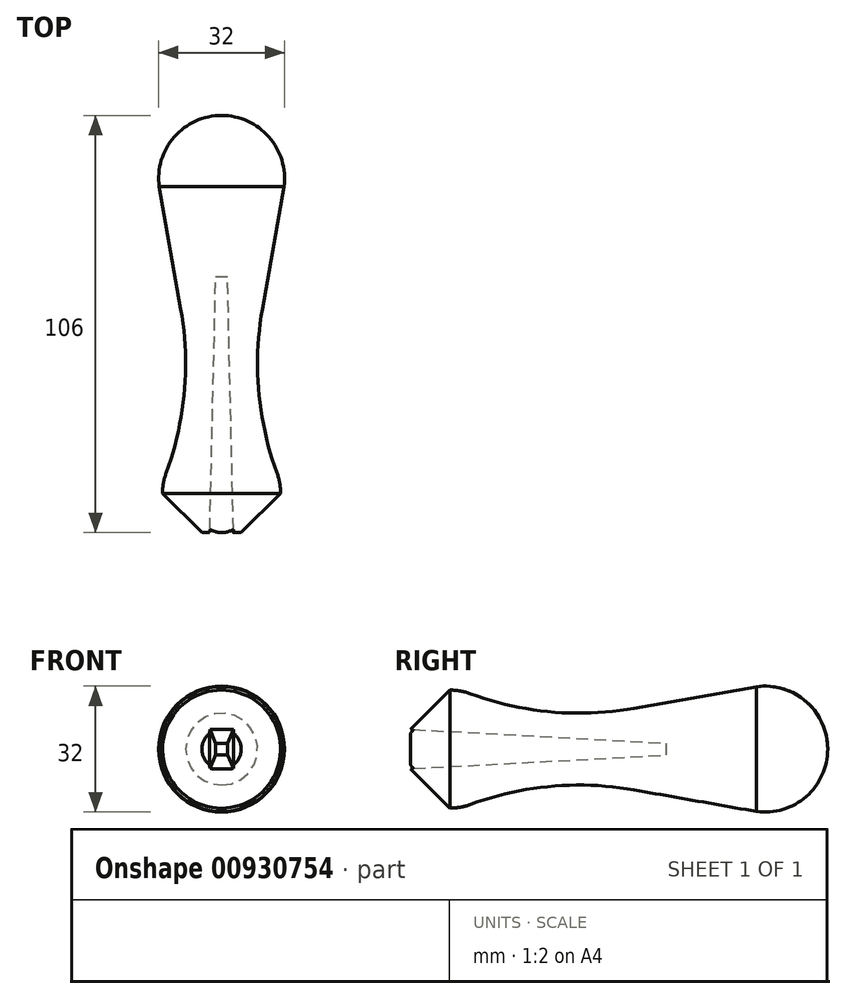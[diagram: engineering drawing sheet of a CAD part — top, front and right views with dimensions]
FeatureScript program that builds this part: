
annotation { "Feature Type Name" : "Feature", "Feature Type Description" : "" }
export const myFeature = defineFeature(function(context is Context, id is Id, definition is map)
    precondition{}
    {
        {
            var Q0;
            Q0=qCreatedBy(makeId("Front.planeOp"),FACE);
            var sketch = newSketch(context, id + "F0", { "sketchPlane" : qUnion([Q0])});
            skLineSegment(sketch, "E0.bottom", {"start": v(3, -5) * mm, "end": v(-3, -5) * mm});
            skLineSegment(sketch, "E0.top", {"start": v(3, 5) * mm, "end": v(-3, 5) * mm});
            skLineSegment(sketch, "E0.left", {"start": v(3, -5) * mm, "end": v(3, 5) * mm});
            skLineSegment(sketch, "E0.right", {"start": v(-3, -5) * mm, "end": v(-3, 5) * mm});
            skPoint(sketch, "E0.middle", {"position": v(0, 0) * mm});
            skSolve(sketch);
        }
        {
            var Q0;
            Q0=makeQuery(id+"F0.imprint","IMPRINT",FACE,{"disambiguationData":[TD([[makeQuery(id+"F0.imprint","IMPRINT",EDGE,{"derivedFrom":sQuery(id+"F0.wireOp",EDGE,"E0.bottom")}),-1.0]])]});
            cPlane(context, id + "F1", {"entities" : qUnion([Q0]), "cplaneType" : CPlaneType.OFFSET, "offset" : 65 * mm, "oppositeDirection" : true, "width" : 150 * mm, "height" : 150 * mm});
        }
        {
            var Q0;
            Q0=qCreatedBy(id+"F1.planeOp",FACE);
            var sketch = newSketch(context, id + "F2", { "sketchPlane" : qUnion([Q0])});
            skLineSegment(sketch, "E1.bottom", {"start": v(1.5, -1.5) * mm, "end": v(-1.5, -1.5) * mm});
            skLineSegment(sketch, "E1.top", {"start": v(1.5, 1.5) * mm, "end": v(-1.5, 1.5) * mm});
            skLineSegment(sketch, "E1.left", {"start": v(1.5, -1.5) * mm, "end": v(1.5, 1.5) * mm});
            skLineSegment(sketch, "E1.right", {"start": v(-1.5, -1.5) * mm, "end": v(-1.5, 1.5) * mm});
            skPoint(sketch, "E1.middle", {"position": v(0, 0) * mm});
            skSolve(sketch);
        }
        {
            var Q0;
            Q0 = qSketchRegion(id + "F0", true);
            var Q1;
            Q1 = qSketchRegion(id + "F2", true);
            loft(context, id + "F3", {"sheetProfilesArray" : [{ "sheetProfileEntities" : qUnion([Q0]) }, { "sheetProfileEntities" : qUnion([Q1]) }]});
        }
        {
            var Q0;
            Q0=qCreatedBy(makeId("Right.planeOp"),FACE);
            var sketch = newSketch(context, id + "F4", { "sketchPlane" : qUnion([Q0])});
            skLineSegment(sketch, "E2", {"start": v(0, 5) * mm, "end": v(10, 15) * mm});
            skLineSegment(sketch, "E3", {"start": v(87.87, 15.86) * mm, "end": v(56.8, 10.36) * mm});
            skArc(sketch, "E4", {"start": v(15.19, 14.07) * mm, "mid": v(12.64, 14.77) * mm, "end": v(10, 15) * mm});
            skArc(sketch, "E5", {"start": v(106, 0) * mm, "mid": v(100.53, 12.04) * mm, "end": v(87.87, 15.86) * mm});
            skArc(sketch, "E6", {"start": v(15.19, 14.07) * mm, "mid": v(35.75, 9.45) * mm, "end": v(56.8, 10.36) * mm});
            skLineSegment(sketch, "E7", {"start": v(0, 5) * mm, "end": v(0, 0) * mm});
            skLineSegment(sketch, "E8", {"start": v(0, 0) * mm, "end": v(106, 0) * mm});
            skSolve(sketch);
        }
        {
            var Q0;
            Q0 = qSketchRegion(id + "F4", true);
            var Q1;
            Q1=sQuery(id+"F4.wireOp",EDGE,"E2");
            var Q2;
            Q2=sQuery(id+"F4.wireOp",EDGE,"E5");
            var Q3;
            Q3=sQuery(id+"F4.wireOp",EDGE,"E6");
            var Q4;
            Q4=sQuery(id+"F4.wireOp",EDGE,"E8");
            var Q5;
            Q5=sQuery(id+"F4.wireOp",EDGE,"E3");
            var Q6;
            Q6=sQuery(id+"F4.wireOp",EDGE,"E7");
            var Q7;
            Q7=sQuery(id+"F4.wireOp",EDGE,"E4");
            var Q8;
            Q8=sQuery(id+"F4.wireOp",EDGE,"E8");
            revolve(context, id + "F5", {"surfaceOperationType" : NewSurfaceOperationType.NEW, "entities" : qUnion([Q0]), "surfaceEntities" : qUnion([Q1, Q2, Q3, Q4, Q5, Q6, Q7]), "axis" : qUnion([Q8]), "revolveType" : RevolveType.FULL});
        }
        {
            var Q0;
            Q0=makeQuery(id+"F3.opLoft","SWEPT_BODY",BODY,{"disambiguationData":[OSD([makeQuery(id+"F0.imprint","IMPRINT",FACE,{"disambiguationData":[TD([[makeQuery(id+"F0.imprint","IMPRINT",EDGE,{"derivedFrom":sQuery(id+"F0.wireOp",EDGE,"E0.bottom")}),-1.0]])]}),makeQuery(id+"F2.imprint","IMPRINT",FACE,{"disambiguationData":[TD([[makeQuery(id+"F2.imprint","IMPRINT",EDGE,{"derivedFrom":sQuery(id+"F2.wireOp",EDGE,"E1.bottom")}),-1.0]])]})])]});
            var Q1;
            Q1=makeQuery(id+"F5.opRevolve","SWEPT_BODY",BODY,{"disambiguationData":[OSD([sQuery(id+"F4.wireOp",EDGE,"E2"),sQuery(id+"F4.wireOp",EDGE,"E3"),sQuery(id+"F4.wireOp",EDGE,"E4"),sQuery(id+"F4.wireOp",EDGE,"E5"),sQuery(id+"F4.wireOp",EDGE,"E6"),sQuery(id+"F4.wireOp",EDGE,"E7"),sQuery(id+"F4.wireOp",EDGE,"E8")])]});
            booleanBodies(context, id + "F6", {"operationType" : BooleanOperationType.SUBTRACTION, "tools" : qUnion([Q0]), "targets" : qUnion([Q1])});
        }
    });
